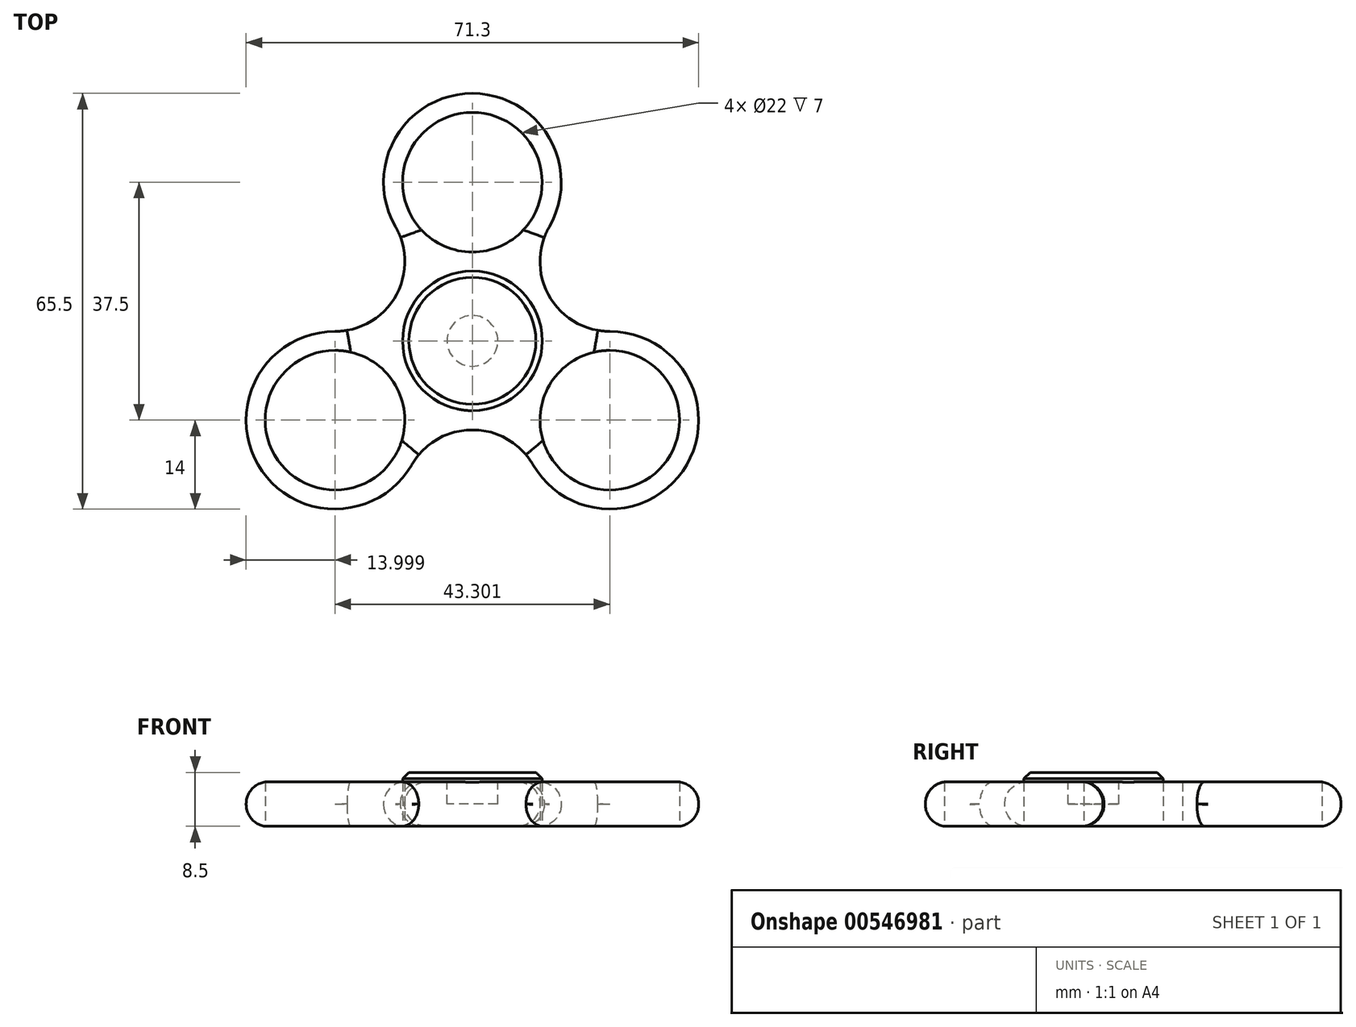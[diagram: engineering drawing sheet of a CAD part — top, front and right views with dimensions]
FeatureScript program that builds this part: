
annotation { "Feature Type Name" : "Feature", "Feature Type Description" : "" }
export const myFeature = defineFeature(function(context is Context, id is Id, definition is map)
    precondition{}
    {
        {
            var Q0;
            Q0=qCreatedBy(makeId("Top.planeOp"),FACE);
            var sketch = newSketch(context, id + "F0", { "sketchPlane" : qUnion([Q0])});
            skCircle(sketch, "E0", {"center": v(0, 0) * mm, "radius": 39 * mm, "construction": true});
            skCircle(sketch, "E1", {"center": v(0, 0) * mm, "radius": 25 * mm, "construction": true});
            skCircle(sketch, "E2", {"center": v(0, 0) * mm, "radius": 11 * mm});
            skCircle(sketch, "E3", {"center": v(0, 25) * mm, "radius": 11 * mm});
            skArc(sketch, "E4.1.0", {"start": v(-21.65, 1.5) * mm, "mid": v(-12.12, 7) * mm, "end": v(-12.12, 18) * mm});
            skCircle(sketch, "E4.2.0", {"center": v(-21.65, -12.5) * mm, "radius": 11 * mm});
            skArc(sketch, "E4.3.0", {"start": v(9.53, -19.5) * mm, "mid": v(0, -14) * mm, "end": v(-9.53, -19.5) * mm});
            skCircle(sketch, "E4.4.0", {"center": v(21.65, -12.5) * mm, "radius": 11 * mm});
            skArc(sketch, "E4.5.0", {"start": v(12.12, 18) * mm, "mid": v(12.12, 7) * mm, "end": v(21.65, 1.5) * mm});
            skArc(sketch, "E5", {"start": v(12.12, 18) * mm, "mid": v(0, 39) * mm, "end": v(-12.12, 18) * mm});
            skArc(sketch, "E6", {"start": v(-21.65, 1.5) * mm, "mid": v(-33.77, -19.5) * mm, "end": v(-9.53, -19.5) * mm});
            skArc(sketch, "E7", {"start": v(9.53, -19.5) * mm, "mid": v(33.77, -19.5) * mm, "end": v(21.65, 1.5) * mm});
            skSolve(sketch);
        }
        {
            var Q0;
            Q0=makeQuery(id+"F0.imprint","IMPRINT",FACE,{"disambiguationData":[TD([[makeQuery(id+"F0.imprint","IMPRINT",EDGE,{"derivedFrom":sQuery(id+"F0.wireOp",EDGE,"E2")}),-1.0]])]});
            extrude(context, id + "F1", {"entities" : qUnion([Q0]), "depth" : 7 * mm, "offsetDistance" : 25 * mm});
        }
        {
            var Q0;
            Q0=makeQuery(id+"F1.opExtrude","SWEPT_FACE",FACE,{"disambiguationData":[OSD([sQuery(id+"F0.wireOp",EDGE,"E5")])]});
            fillet(context, id + "F2", {"entities" : qUnion([Q0]), "radius" : 3.5 * mm, "tangentPropagation" : true, "allowEdgeOverflow" : false});
        }
        {
            var Q0;
            Q0=makeQuery(id+"F2.opFillet","SPLIT",FACE,{"disambiguationData":[OD(2.0)],"derivedFrom":makeQuery(id+"F1.opExtrude","CAP_FACE",FACE,{"disambiguationData":[OSD([sQuery(id+"F0.wireOp",EDGE,"E2"),sQuery(id+"F0.wireOp",EDGE,"E3"),sQuery(id+"F0.wireOp",EDGE,"E4.1.0"),sQuery(id+"F0.wireOp",EDGE,"E4.2.0"),sQuery(id+"F0.wireOp",EDGE,"E4.3.0"),sQuery(id+"F0.wireOp",EDGE,"E4.4.0"),sQuery(id+"F0.wireOp",EDGE,"E4.5.0"),sQuery(id+"F0.wireOp",EDGE,"E5"),sQuery(id+"F0.wireOp",EDGE,"E6"),sQuery(id+"F0.wireOp",EDGE,"E7")])],"isStart":false})});
            var sketch = newSketch(context, id + "F3", { "sketchPlane" : qUnion([Q0])});
            skLineSegment(sketch, "E8.0", {"start": v(8.04, 7.51) * mm, "end": v(8.04, 7.51) * mm});
            skArc(sketch, "E9", {"start": v(-8.04, 7.51) * mm, "mid": v(0, 11) * mm, "end": v(8.04, 7.51) * mm, "construction": true});
            skArc(sketch, "E10", {"start": v(10.52, 3.2) * mm, "mid": v(9.53, -5.5) * mm, "end": v(2.49, -10.72) * mm, "construction": true});
            skArc(sketch, "E11", {"start": v(-2.49, -10.71) * mm, "mid": v(-9.53, -5.5) * mm, "end": v(-10.52, 3.2) * mm, "construction": true});
            skCircle(sketch, "E12", {"center": v(0, 0) * mm, "radius": 4 * mm});
            skCircle(sketch, "E13", {"center": v(0, 0) * mm, "radius": 11 * mm});
            skSolve(sketch);
        }
        {
            var Q0;
            Q0=makeQuery(id+"F3.imprint","IMPRINT",FACE,{"disambiguationData":[TD([[makeQuery(id+"F3.imprint","IMPRINT",EDGE,{"derivedFrom":sQuery(id+"F3.wireOp",EDGE,"E12")}),1.0]])]});
            extrude(context, id + "F4", {"entities" : qUnion([Q0]), "oppositeDirection" : true, "depth" : 3.5 * mm, "offsetDistance" : 25 * mm});
        }
        {
            var Q0;
            Q0=makeQuery(id+"F3.imprint","IMPRINT",FACE,{"disambiguationData":[TD([[makeQuery(id+"F3.imprint","IMPRINT",EDGE,{"derivedFrom":sQuery(id+"F3.wireOp",EDGE,"E12")}),-1.0]])]});
            var Q1;
            Q1=makeQuery(id+"F3.imprint","IMPRINT",FACE,{"disambiguationData":[TD([[makeQuery(id+"F3.imprint","IMPRINT",EDGE,{"derivedFrom":sQuery(id+"F3.wireOp",EDGE,"E12")}),1.0]])]});
            extrude(context, id + "F5", {"entities" : qUnion([Q0, Q1]), "operationType" : NewBodyOperationType.ADD, "depth" : 1.5 * mm, "offsetDistance" : 25 * mm});
        }
        {
            var Q0;
            Q0=makeQuery(id+"F5.opExtrude","CAP_EDGE",EDGE,{"disambiguationData":[OSD([sQuery(id+"F3.wireOp",EDGE,"E13")])],"isStart":false});
            chamfer(context, id + "F6", {"entities" : qUnion([Q0]), "width" : 1 * mm, "tangentPropagation" : true});
        }
    });
